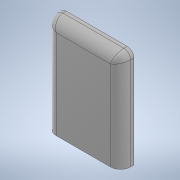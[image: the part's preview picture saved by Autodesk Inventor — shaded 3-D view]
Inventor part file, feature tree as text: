
AUTODESK INVENTOR PART (.ipt)
format: ipt  version: 2020 (Build 240168000, 168)  size: 124,928 bytes
history: native  units: in
note: dims shown in document units (in); Inventor stores cm internally (conversion verified against a paired STEP export)
features: fillet x2, extrude x1, sketch x1
ambient origin geometry x8: Origin, YZ Plane, XZ Plane, XY Plane, X Axis, Y Axis, Z Axis, Center Point
bodies: Solid1 (feature_tree)
feature tree (4):
  extrude  "Extrusion1"  Depth=14.688in
  fillet  "Fillet1"  Radius=2.0in
  fillet  "Fillet2"  Radius=1.0in
  sketch  "Sketch1"  dims[d0=11.0in d1=14.688in d2=2.0in d3=0.0in d4=1.0in d5=1.5in]
